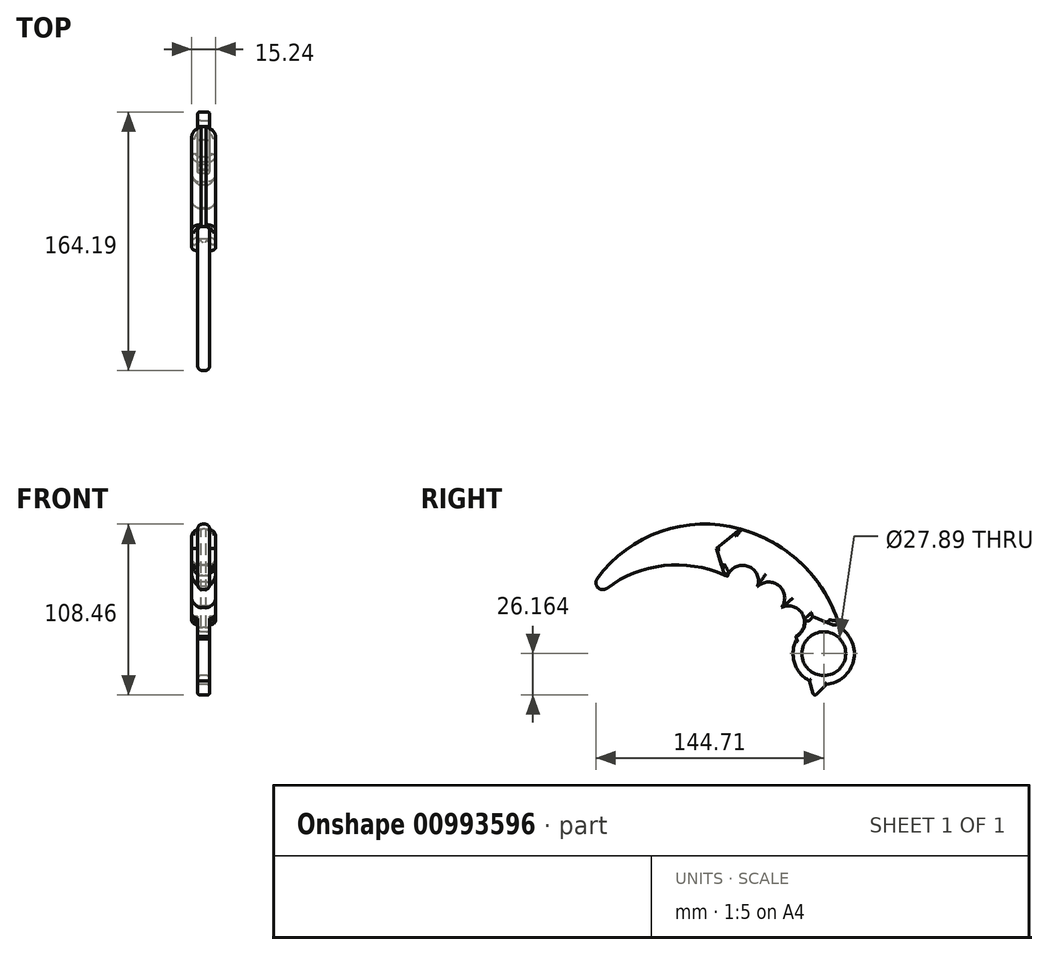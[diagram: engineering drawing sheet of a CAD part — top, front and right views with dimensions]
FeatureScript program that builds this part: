
annotation { "Feature Type Name" : "Feature", "Feature Type Description" : "" }
export const myFeature = defineFeature(function(context is Context, id is Id, definition is map)
    precondition{}
    {
        {
            var Q0;
            Q0=qCreatedBy(makeId("Right.planeOp"),FACE);
            var sketch = newSketch(context, id + "F0", { "sketchPlane" : qUnion([Q0])});
            skArc(sketch, "E0", {"start": v(5.32, 16.36) * mm, "mid": v(-47.52, 19.44) * mm, "end": v(-88.8, -13.7) * mm});
            skArc(sketch, "E1", {"start": v(51.17, -24.15) * mm, "mid": v(33.33, 1.86) * mm, "end": v(5.32, 16.36) * mm});
            skArc(sketch, "E2", {"start": v(51.17, -24.15) * mm, "mid": v(73.29, -52.28) * mm, "end": v(78.56, -16.89) * mm});
            skArc(sketch, "E3", {"start": v(15.2, 45.7) * mm, "mid": v(-49.24, 37.78) * mm, "end": v(-88.8, -13.7) * mm});
            skArc(sketch, "E4", {"start": v(78.56, -16.89) * mm, "mid": v(55.14, 22.77) * mm, "end": v(15.2, 45.7) * mm});
            skLineSegment(sketch, "E5", {"start": v(5.32, 16.36) * mm, "end": v(0, 33.43) * mm});
            skLineSegment(sketch, "E6", {"start": v(0, 33.43) * mm, "end": v(15.2, 45.7) * mm});
            skLineSegment(sketch, "E7", {"start": v(51.17, -24.15) * mm, "end": v(61.16, -9.91) * mm});
            skLineSegment(sketch, "E8", {"start": v(61.16, -9.91) * mm, "end": v(78.56, -16.89) * mm});
            skCircle(sketch, "E9", {"center": v(68.3, -33.45) * mm, "radius": 13.94 * mm});
            skLineSegment(sketch, "E10", {"start": v(69.92, -52.86) * mm, "end": v(62.15, -60.72) * mm});
            skLineSegment(sketch, "E11", {"start": v(62.15, -60.72) * mm, "end": v(59.13, -50.64) * mm});
            skLineSegment(sketch, "E12", {"start": v(59.13, -50.64) * mm, "end": v(69.92, -52.86) * mm});
            skCircle(sketch, "E13", {"center": v(16.7, 12.53) * mm, "radius": 10.16 * mm});
            skCircle(sketch, "E14", {"center": v(33.33, 1.86) * mm, "radius": 10.16 * mm});
            skCircle(sketch, "E15", {"center": v(45.96, -13.32) * mm, "radius": 10.16 * mm});
            skSolve(sketch);
        }
        {
            var Q0;
            {var subQ1=sQuery(id+"F0.wireOp",EDGE,"E5");Q0=makeQuery(id+"F0.imprint","IMPRINT",FACE,{"disambiguationData":[TD([[makeQuery(id+"F0.imprint","IMPRINT",EDGE,{"derivedFrom":subQ1}),-1.0]])]});}
            extrude(context, id + "F1", {"entities" : qUnion([Q0]), "depth" : 7.62 * mm, "offsetDistance" : 25.4 * mm, "hasSecondDirection" : true, "secondDirectionOppositeDirection" : true, "secondDirectionDepth" : 7.62 * mm});
        }
        {
            var Q0;
            Q0=makeQuery(id+"F0.imprint","IMPRINT",FACE,{"disambiguationData":[TD([[makeQuery(id+"F0.imprint","IMPRINT",EDGE,{"derivedFrom":sQuery(id+"F0.wireOp",EDGE,"E0")}),-1.0]])]});
            var Q1;
            {var subQ1=sQuery(id+"F0.wireOp",EDGE,"E7");Q1=makeQuery(id+"F0.imprint","IMPRINT",FACE,{"disambiguationData":[TD([[makeQuery(id+"F0.imprint","IMPRINT",EDGE,{"derivedFrom":subQ1}),-1.0]])]});}
            var Q2;
            {var subQ0=sQuery(id+"F0.wireOp",EDGE,"E12");Q2=makeQuery(id+"F0.imprint","IMPRINT",FACE,{"disambiguationData":[TD([[makeQuery(id+"F0.imprint","IMPRINT",EDGE,{"derivedFrom":subQ0}),-1.0]])]});}
            var Q3;
            {var subQ1=sQuery(id+"F0.wireOp",EDGE,"E10");Q3=makeQuery(id+"F0.imprint","IMPRINT",FACE,{"disambiguationData":[TD([[makeQuery(id+"F0.imprint","IMPRINT",EDGE,{"derivedFrom":subQ1}),-1.0]])]});}
            extrude(context, id + "F2", {"entities" : qUnion([Q0, Q1, Q2, Q3]), "operationType" : NewBodyOperationType.ADD, "depth" : 3.8 * mm, "offsetDistance" : 25.4 * mm, "hasSecondDirection" : true, "secondDirectionOppositeDirection" : true, "secondDirectionDepth" : 3.8 * mm});
        }
        {
            var Q0;
            Q0=makeQuery(id+"F1.opExtrude","CAP_EDGE",EDGE,{"disambiguationData":[OSD([sQuery(id+"F0.wireOp",EDGE,"E13")])],"isStart":false});
            var Q1;
            Q1=makeQuery(id+"F1.opExtrude","CAP_EDGE",EDGE,{"disambiguationData":[OSD([sQuery(id+"F0.wireOp",EDGE,"E13")])],"isStart":true});
            var Q2;
            Q2=makeQuery(id+"F1.opExtrude","CAP_EDGE",EDGE,{"disambiguationData":[OSD([sQuery(id+"F0.wireOp",EDGE,"E14")])],"isStart":true});
            var Q3;
            Q3=makeQuery(id+"F1.opExtrude","CAP_EDGE",EDGE,{"disambiguationData":[OSD([sQuery(id+"F0.wireOp",EDGE,"E15")])],"isStart":true});
            var Q4;
            Q4=makeQuery(id+"F1.opExtrude","CAP_EDGE",EDGE,{"disambiguationData":[OSD([sQuery(id+"F0.wireOp",EDGE,"E15")])],"isStart":false});
            var Q5;
            Q5=makeQuery(id+"F1.opExtrude","CAP_EDGE",EDGE,{"disambiguationData":[OSD([sQuery(id+"F0.wireOp",EDGE,"E14")])],"isStart":false});
            fillet(context, id + "F3", {"entities" : qUnion([Q0, Q1, Q2, Q3, Q4, Q5]), "radius" : 5.33 * mm, "tangentPropagation" : true, "allowEdgeOverflow" : false});
        }
        {
            var Q0;
            Q0=makeQuery(id+"F1.opExtrude","CAP_EDGE",EDGE,{"disambiguationData":[OSD([sQuery(id+"F0.wireOp",EDGE,"E4")])],"isStart":false});
            var Q1;
            Q1=makeQuery(id+"F1.opExtrude","CAP_EDGE",EDGE,{"disambiguationData":[OSD([sQuery(id+"F0.wireOp",EDGE,"E4")])],"isStart":true});
            fillet(context, id + "F4", {"entities" : qUnion([Q0, Q1]), "radius" : 5.08 * mm, "tangentPropagation" : true, "allowEdgeOverflow" : false});
        }
        {
            var Q0;
            Q0=makeQuery(id+"F1.opExtrude","CAP_EDGE",EDGE,{"disambiguationData":[OSD([sQuery(id+"F0.wireOp",EDGE,"E6")])],"isStart":false});
            var Q1;
            Q1=makeQuery(id+"F1.opExtrude","CAP_EDGE",EDGE,{"disambiguationData":[OSD([sQuery(id+"F0.wireOp",EDGE,"E5")])],"isStart":false});
            var Q2;
            Q2=makeQuery(id+"F1.opExtrude","CAP_EDGE",EDGE,{"disambiguationData":[OSD([sQuery(id+"F0.wireOp",EDGE,"E5")])],"isStart":true});
            var Q3;
            Q3=makeQuery(id+"F1.opExtrude","CAP_EDGE",EDGE,{"disambiguationData":[OSD([sQuery(id+"F0.wireOp",EDGE,"E6")])],"isStart":true});
            var Q4;
            Q4=makeQuery(id+"F1.opExtrude","CAP_EDGE",EDGE,{"disambiguationData":[OSD([sQuery(id+"F0.wireOp",EDGE,"E7")])],"isStart":false});
            var Q5;
            Q5=makeQuery(id+"F1.opExtrude","CAP_EDGE",EDGE,{"disambiguationData":[OSD([sQuery(id+"F0.wireOp",EDGE,"E8")])],"isStart":false});
            var Q6;
            Q6=makeQuery(id+"F1.opExtrude","CAP_EDGE",EDGE,{"disambiguationData":[OSD([sQuery(id+"F0.wireOp",EDGE,"E8")])],"isStart":true});
            var Q7;
            Q7=makeQuery(id+"F1.opExtrude","CAP_EDGE",EDGE,{"disambiguationData":[OSD([sQuery(id+"F0.wireOp",EDGE,"E7")])],"isStart":true});
            var Q8;
            {var subQ0=sQuery(id+"F0.wireOp",EDGE,"E7");var subQ1=sQuery(id+"F0.wireOp",EDGE,"E2");var subQ4=sQuery(id+"F0.wireOp",EDGE,"E11");var subQ5=sQuery(id+"F0.wireOp",EDGE,"E8");var subQ6=sQuery(id+"F0.wireOp",EDGE,"E15");Q8=makeQuery(id+"F3.opFillet","BLEND_EDGE",EDGE,{"blendedFrom":[makeQuery(id+"F1.opExtrude","CAP_EDGE",EDGE,{"disambiguationData":[OSD([subQ6])],"isStart":false}),makeQuery(id+"FhUC5OvBJ4RweXD_1.boolean.opBoolean","SPLIT",FACE,{"disambiguationData":[TD([makeQuery(id+"FhUC5OvBJ4RweXD_1.opExtrude","CAP_FACE",FACE,{"disambiguationData":[OSD([subQ1,subQ0,subQ5,sQuery(id+"F0.wireOp",EDGE,"E9"),sQuery(id+"F0.wireOp",EDGE,"E10"),subQ4])],"isStart":false})])],"derivedFrom":makeQuery(id+"F1.opExtrude","SWEPT_FACE",FACE,{"disambiguationData":[OSD([subQ0])]})})],"blendedInto":[makeQuery(id+"FhUC5OvBJ4RweXD_1.boolean.opBoolean","SPLIT",FACE,{"disambiguationData":[TD([makeQuery(id+"FhUC5OvBJ4RweXD_1.opExtrude","CAP_FACE",FACE,{"disambiguationData":[OSD([subQ1,subQ0,subQ5,sQuery(id+"F0.wireOp",EDGE,"E9"),sQuery(id+"F0.wireOp",EDGE,"E10"),subQ4])],"isStart":false})])],"derivedFrom":makeQuery(id+"F1.opExtrude","SWEPT_FACE",FACE,{"disambiguationData":[OSD([subQ0])]})})]});}
            var Q9;
            {var subQ0=sQuery(id+"F0.wireOp",EDGE,"E7");var subQ1=sQuery(id+"F0.wireOp",EDGE,"E2");var subQ4=sQuery(id+"F0.wireOp",EDGE,"E11");var subQ5=sQuery(id+"F0.wireOp",EDGE,"E8");var subQ6=sQuery(id+"F0.wireOp",EDGE,"E15");Q9=makeQuery(id+"F3.opFillet","BLEND_EDGE",EDGE,{"blendedFrom":[makeQuery(id+"F1.opExtrude","CAP_EDGE",EDGE,{"disambiguationData":[OSD([subQ6])],"isStart":true}),makeQuery(id+"F2.boolean.opBoolean","SPLIT",FACE,{"disambiguationData":[TD([makeQuery(id+"F2.opExtrude","CAP_FACE",FACE,{"disambiguationData":[OSD([subQ1,subQ0,subQ5,sQuery(id+"F0.wireOp",EDGE,"E9"),sQuery(id+"F0.wireOp",EDGE,"E10"),subQ4])],"isStart":true})])],"derivedFrom":makeQuery(id+"F1.opExtrude","SWEPT_FACE",FACE,{"disambiguationData":[OSD([subQ0])]})})],"blendedInto":[makeQuery(id+"F2.boolean.opBoolean","SPLIT",FACE,{"disambiguationData":[TD([makeQuery(id+"F2.opExtrude","CAP_FACE",FACE,{"disambiguationData":[OSD([subQ1,subQ0,subQ5,sQuery(id+"F0.wireOp",EDGE,"E9"),sQuery(id+"F0.wireOp",EDGE,"E10"),subQ4])],"isStart":true})])],"derivedFrom":makeQuery(id+"F1.opExtrude","SWEPT_FACE",FACE,{"disambiguationData":[OSD([subQ0])]})})]});}
            fillet(context, id + "F5", {"entities" : qUnion([Q0, Q1, Q2, Q3, Q4, Q5, Q6, Q7, Q8, Q9]), "radius" : 2.03 * mm, "tangentPropagation" : true, "allowEdgeOverflow" : false});
        }
        {
            var Q0;
            Q0=makeQuery(id+"F2.opExtrude","SWEPT_EDGE",EDGE,{"disambiguationData":[OSD([sQuery(id+"F0.wireOp",EDGE,"E0"),sQuery(id+"F0.wireOp",EDGE,"E3")])]});
            fillet(context, id + "F6", {"entities" : qUnion([Q0]), "radius" : 4.36 * mm, "tangentPropagation" : true, "allowEdgeOverflow" : false});
        }
        {
            var Q0;
            Q0=makeQuery(id+"F2.opExtrude","CAP_EDGE",EDGE,{"disambiguationData":[OSD([sQuery(id+"F0.wireOp",EDGE,"E0")])],"isStart":true});
            var Q1;
            Q1=makeQuery(id+"F2.opExtrude","SWEPT_FACE",FACE,{"disambiguationData":[OSD([sQuery(id+"F0.wireOp",EDGE,"E0")])]});
            fillet(context, id + "F7", {"entities" : qUnion([Q0, Q1]), "radius" : 3.07 * mm, "tangentPropagation" : true, "allowEdgeOverflow" : false});
        }
        {
            var Q0;
            Q0=makeQuery(id+"F2.opExtrude","CAP_EDGE",EDGE,{"disambiguationData":[OSD([sQuery(id+"F0.wireOp",EDGE,"E9")])],"isStart":true});
            var Q1;
            Q1=makeQuery(id+"F2.opExtrude","CAP_EDGE",EDGE,{"disambiguationData":[OSD([sQuery(id+"F0.wireOp",EDGE,"E9")])],"isStart":false});
            fillet(context, id + "F8", {"entities" : qUnion([Q0, Q1]), "radius" : 1.84 * mm, "tangentPropagation" : true, "allowEdgeOverflow" : false});
        }
        {
            var Q0;
            {var subQ0=sQuery(id+"F0.wireOp",EDGE,"E2");Q0=makeQuery(id+"F2.opExtrude","CAP_EDGE",EDGE,{"disambiguationData":[OSD([subQ0]),TDD([makeQuery(id+"F0.imprint","IMPRINT",EDGE,{"disambiguationData":[TD([[makeQuery(id+"F0.imprint","INTERSECT",VERTEX,{"derivedFrom":[subQ0,sQuery(id+"F0.wireOp",EDGE,"E4"),sQuery(id+"F0.wireOp",EDGE,"E8")]}),1.0]])],"derivedFrom":subQ0})])],"isStart":false});}
            var Q1;
            Q1=makeQuery(id+"F2.opExtrude","CAP_EDGE",EDGE,{"disambiguationData":[OSD([sQuery(id+"F0.wireOp",EDGE,"E10")])],"isStart":false});
            var Q2;
            Q2=makeQuery(id+"F2.opExtrude","SWEPT_EDGE",EDGE,{"disambiguationData":[OSD([sQuery(id+"F0.wireOp",EDGE,"E10"),sQuery(id+"F0.wireOp",EDGE,"E11")])]});
            var Q3;
            Q3=makeQuery(id+"F2.opExtrude","CAP_EDGE",EDGE,{"disambiguationData":[OSD([sQuery(id+"F0.wireOp",EDGE,"E11")])],"isStart":false});
            var Q4;
            {var subQ0=sQuery(id+"F0.wireOp",EDGE,"E2");Q4=makeQuery(id+"F2.opExtrude","CAP_EDGE",EDGE,{"disambiguationData":[OSD([subQ0]),TDD([makeQuery(id+"F0.imprint","IMPRINT",EDGE,{"disambiguationData":[TD([[makeQuery(id+"F0.imprint","INTERSECT",VERTEX,{"derivedFrom":[sQuery(id+"F0.wireOp",EDGE,"E1"),subQ0,sQuery(id+"F0.wireOp",EDGE,"E7")]}),-1.0]])],"derivedFrom":subQ0})])],"isStart":false});}
            var Q5;
            {var subQ0=sQuery(id+"F0.wireOp",EDGE,"E2");Q5=makeQuery(id+"F2.opExtrude","CAP_EDGE",EDGE,{"disambiguationData":[OSD([subQ0]),TDD([makeQuery(id+"F0.imprint","IMPRINT",EDGE,{"disambiguationData":[TD([[makeQuery(id+"F0.imprint","INTERSECT",VERTEX,{"derivedFrom":[sQuery(id+"F0.wireOp",EDGE,"E1"),subQ0,sQuery(id+"F0.wireOp",EDGE,"E7")]}),-1.0]])],"derivedFrom":subQ0})])],"isStart":true});}
            var Q6;
            Q6=makeQuery(id+"F2.opExtrude","CAP_EDGE",EDGE,{"disambiguationData":[OSD([sQuery(id+"F0.wireOp",EDGE,"E10")])],"isStart":true});
            var Q7;
            Q7=makeQuery(id+"F2.opExtrude","CAP_EDGE",EDGE,{"disambiguationData":[OSD([sQuery(id+"F0.wireOp",EDGE,"E11")])],"isStart":true});
            var Q8;
            {var subQ0=sQuery(id+"F0.wireOp",EDGE,"E2");Q8=makeQuery(id+"F2.opExtrude","CAP_EDGE",EDGE,{"disambiguationData":[OSD([subQ0]),TDD([makeQuery(id+"F0.imprint","IMPRINT",EDGE,{"disambiguationData":[TD([[makeQuery(id+"F0.imprint","INTERSECT",VERTEX,{"derivedFrom":[subQ0,sQuery(id+"F0.wireOp",EDGE,"E4"),sQuery(id+"F0.wireOp",EDGE,"E8")]}),1.0]])],"derivedFrom":subQ0})])],"isStart":true});}
            fillet(context, id + "F9", {"entities" : qUnion([Q0, Q1, Q2, Q3, Q4, Q5, Q6, Q7, Q8]), "radius" : 1.23 * mm, "tangentPropagation" : true, "allowEdgeOverflow" : false});
        }
    });
